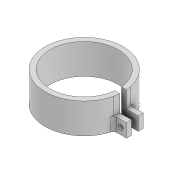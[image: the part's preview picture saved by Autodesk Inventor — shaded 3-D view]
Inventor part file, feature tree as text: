
AUTODESK INVENTOR PART (.ipt)
format: ipt  version: 2022 (Build 260153000, 153)  size: 139,776 bytes
history: native  units: mm
features: extrude x3, sketch x3, fillet x1, projected_geometry x1
ambient origin geometry x8: Origin, YZ Plane, XZ Plane, XY Plane, X Axis, Y Axis, Z Axis, Center Point
bodies: Solid1 (feature_tree)
feature tree (8):
  extrude  "Extrusion1"  Depth=3.0mm
  extrude  "Extrusion2"  Depth=2.0mm
  extrude  "Extrusion3"  Depth=18.0mm TaperAngle=0.0deg
  fillet  "Fillet1"  Radius=10.0mm
  sketch  "Sketch1"  dims[d0=40.5mm d2=3.0mm]
  sketch  "Sketch2"  dims[d3=3.0mm d4=2.0mm]
  projected_geometry  "Projected Loop1"
  sketch  "Sketch3"  dims[d5=10.0mm d6=18.0mm d7=0.0mm d8=10.0mm d9=0.0mm d11=3.2mm d12=4.0mm d14=22.0mm d15=0.0mm d16=2.0mm d17=3.0mm]
